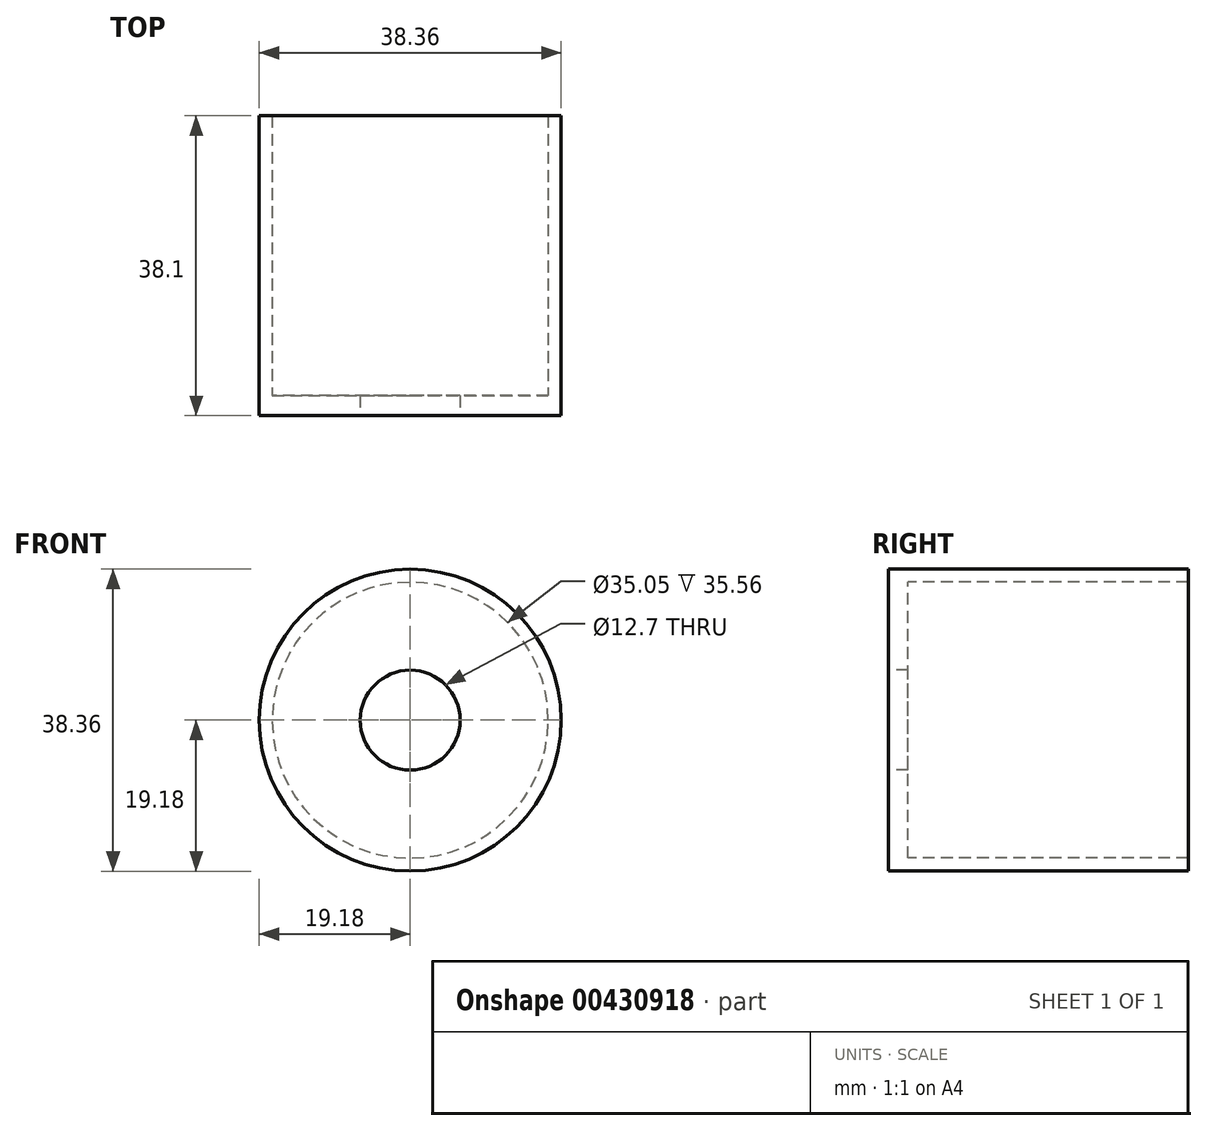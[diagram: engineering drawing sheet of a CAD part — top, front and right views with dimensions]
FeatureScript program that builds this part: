
annotation { "Feature Type Name" : "Feature", "Feature Type Description" : "" }
export const myFeature = defineFeature(function(context is Context, id is Id, definition is map)
    precondition{}
    {
        {
            var Q0;
            Q0=qCreatedBy(makeId("Front.planeOp"),FACE);
            var sketch = newSketch(context, id + "F0", { "sketchPlane" : qUnion([Q0])});
            skCircle(sketch, "E0", {"center": v(0, 0) * mm, "radius": 19.18 * mm});
            skCircle(sketch, "E1", {"center": v(0, 0) * mm, "radius": 17.53 * mm});
            skSolve(sketch);
        }
        {
            var Q0;
            Q0=makeQuery(id+"F0.imprint","IMPRINT",FACE,{"disambiguationData":[TD([[makeQuery(id+"F0.imprint","IMPRINT",EDGE,{"derivedFrom":sQuery(id+"F0.wireOp",EDGE,"E0")}),1.0]])]});
            var Q1;
            Q1=sQuery(id+"F0.wireOp",EDGE,"E1");
            var Q2;
            Q2=sQuery(id+"F0.wireOp",EDGE,"E0");
            extrude(context, id + "F1", {"entities" : qUnion([Q0]), "surfaceEntities" : qUnion([Q1, Q2]), "oppositeDirection" : true, "depth" : 38.1 * mm});
        }
        {
            var Q0;
            Q0=qCreatedBy(makeId("Front.planeOp"),FACE);
            var sketch = newSketch(context, id + "F2", { "sketchPlane" : qUnion([Q0])});
            skCircle(sketch, "E2", {"center": v(0, 0) * mm, "radius": 17.53 * mm});
            skSolve(sketch);
        }
        {
            var Q0;
            Q0=makeQuery(id+"F2.imprint","IMPRINT",FACE,{"disambiguationData":[TD([[makeQuery(id+"F2.imprint","IMPRINT",EDGE,{"derivedFrom":sQuery(id+"F2.wireOp",EDGE,"E2")}),1.0]])]});
            extrude(context, id + "F3", {"entities" : qUnion([Q0]), "operationType" : NewBodyOperationType.ADD, "oppositeDirection" : true, "depth" : 2.54 * mm});
        }
        {
            var Q0;
            Q0=makeQuery(id+"F3.opExtrude","CAP_FACE",FACE,{"disambiguationData":[OSD([sQuery(id+"F2.wireOp",EDGE,"E2")])],"isStart":true});
            var sketch = newSketch(context, id + "F4", { "sketchPlane" : qUnion([Q0])});
            skCircle(sketch, "E3", {"center": v(0, 0) * mm, "radius": 6.35 * mm});
            skSolve(sketch);
        }
        {
            var Q0;
            Q0=makeQuery(id+"F4.imprint","IMPRINT",FACE,{"disambiguationData":[TD([[makeQuery(id+"F4.imprint","IMPRINT",EDGE,{"derivedFrom":sQuery(id+"F4.wireOp",EDGE,"E3")}),1.0]])]});
            extrude(context, id + "F5", {"entities" : qUnion([Q0]), "operationType" : NewBodyOperationType.REMOVE, "oppositeDirection" : true, "depth" : 25.4 * mm});
        }
    });
